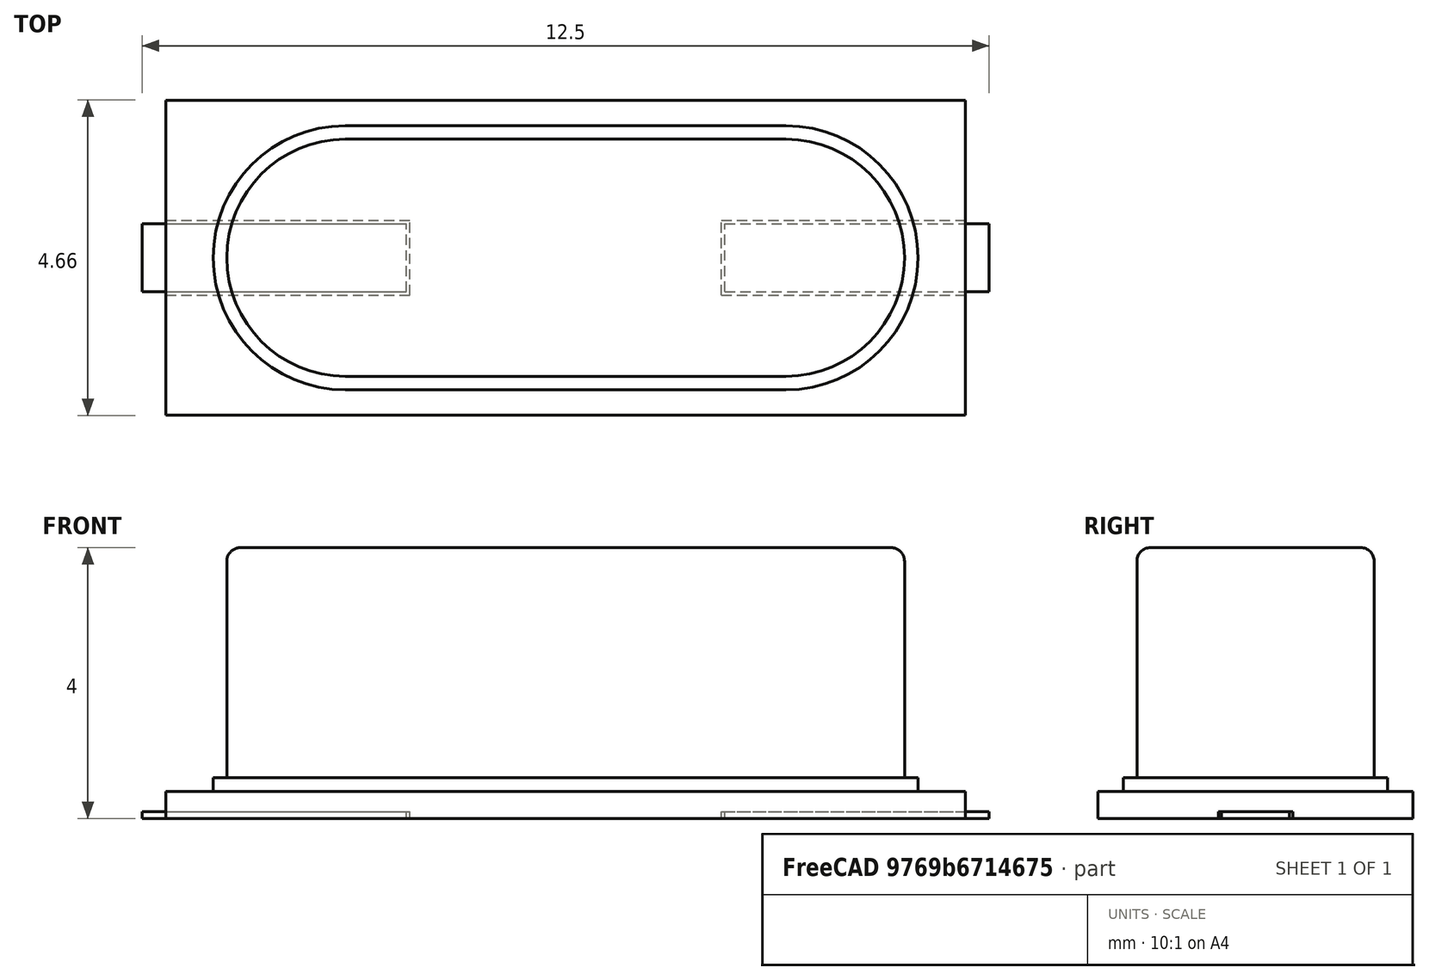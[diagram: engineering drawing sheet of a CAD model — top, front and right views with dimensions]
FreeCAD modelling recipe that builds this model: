
FCSTD DOCUMENT  (FreeCAD 0.18R)
Label: Crystal_SMD_HC49-SD
License: All rights reserved
LicenseURL: http://en.wikipedia.org/wiki/All_rights_reserved
objects: Part::Box×7, Part::Feature×5, Part::Cylinder×4, Part::MultiFuse×2, Part::Cut×2, Part::Fillet×1, App::Part×1, Part::Compound×1
note: 22 computed .brp shape members not serialized (recipe doc carries the construction recipe); baked Part::Feature solids carry a one-line shape summary decoded from their .brp

FEATURE [Part::Box] Box007  label="Pin_R"
  AttacherType = Attacher::AttachEngine3D
  Height = 0.1
  Length = 3.9
  Placement = pos=(2.35,-0.5,0) rot=(0,0,1;0rad)
  Width = 1
FEATURE [Part::Box] Box008  label="Pin_L"
  AttacherType = Attacher::AttachEngine3D
  Height = 0.1
  Length = 3.9
  Placement = pos=(-6.25,-0.5,0) rot=(0,0,1;0rad)
  Width = 1
FEATURE [Part::Box] Box009  label="Cube007"
  AttacherType = Attacher::AttachEngine3D
  Height = 3.4
  Length = 6.5
  Placement = pos=(-3.25,-1.75,0.6) rot=(0,0,1;0rad)
  Width = 3.5
FEATURE [Part::Cylinder] Cylinder004
  Angle = 180
  AttacherType = Attacher::AttachEngine3D
  Height = 3.4
  Placement = pos=(-3.25,0,0.6) rot=(0,0,1;1.5708rad)
  Radius = 1.75
FEATURE [Part::Cylinder] Cylinder005
  Angle = 180
  AttacherType = Attacher::AttachEngine3D
  Height = 3.4
  Placement = pos=(3.25,0,0.6) rot=(0,0,-1;1.5708rad)
  Radius = 1.75
FEATURE [Part::Box] Box010  label="Cube008"
  AttacherType = Attacher::AttachEngine3D
  Height = 0.2
  Length = 6.5
  Placement = pos=(-3.25,-1.95,0.4) rot=(0,0,1;0rad)
  Width = 3.9
FEATURE [Part::Cylinder] Cylinder006
  Angle = 180
  AttacherType = Attacher::AttachEngine3D
  Height = 0.2
  Placement = pos=(-3.25,0,0.4) rot=(0,0,1;1.5708rad)
  Radius = 1.95
FEATURE [Part::Cylinder] Cylinder007
  Angle = 180
  AttacherType = Attacher::AttachEngine3D
  Height = 0.2
  Placement = pos=(3.25,0,0.4) rot=(0,0,-1;1.5708rad)
  Radius = 1.95
FEATURE [Part::MultiFuse] Fusion001
  Shapes = -> [Box009,Cylinder005,Cylinder004,Box010,Cylinder006,Cylinder007]
FEATURE [Part::Fillet] Fillet001  label="Cap"
  Base = -> Fusion001
  Edges = 4 edges r=0.2: [Edge3,Edge8,Edge13,Edge16]
FEATURE [Part::Box] Box011  label="Cube009"
  AttacherType = Attacher::AttachEngine3D
  Height = 0.4
  Length = 11.8
  Placement = pos=(-5.9,-2.325,0) rot=(0,0,1;0rad)
  Width = 4.65
FEATURE [Part::Box] Box012  label="Cube010"
  AttacherType = Attacher::AttachEngine3D
  Height = 0.1
  Length = 4
  Placement = pos=(2.3,-0.55,0) rot=(0,0,1;0rad)
  Width = 1.1
FEATURE [Part::Cut] Cut003
  Base = -> Box011
  Tool = -> Box012
FEATURE [Part::Box] Box013  label="Cube011"
  AttacherType = Attacher::AttachEngine3D
  Height = 0.1
  Length = 4
  Placement = pos=(-6.3,-0.55,0) rot=(0,0,1;0rad)
  Width = 1.1
FEATURE [Part::Cut] Cut002  label="Base"
  Base = -> Cut003
  Tool = -> Box013
FEATURE [App::Part] Part  label="Crystal"
  Group = -> [Box007,Box008,Cylinder005,Fusion001,Box009,Cylinder006,Cylinder007,Box010,Cylinder004,Fillet001,Cut003,Box013,Box012,Box011,Cut002]
  Origin = -> Origin
FEATURE [Part::Feature] Box007_cp  label="Pin_R_cp"
  Placement = pos=(2.35,-0.5,0) rot=(0,0,1;0rad)
  shape: bbox 3.9 x 1 x 0.1 mm, 6 faces (baked)
FEATURE [Part::Feature] Box008_cp  label="Pin_L_cp"
  Placement = pos=(-6.25,-0.5,0) rot=(0,0,1;0rad)
  shape: bbox 3.9 x 1 x 0.1 mm, 6 faces (baked)
FEATURE [Part::Feature] Fillet001_cp  label="Cap_cp"
  shape: bbox 10.4 x 3.9 x 3.6 mm, 22 faces (baked)
FEATURE [Part::Feature] Cut002_cp  label="Base_cp"
  shape: bbox 11.8 x 4.65 x 0.4 mm, 14 faces (baked)
FEATURE [Part::Compound] Crystal_cp
  Links = -> [Box007_cp,Box008_cp,Fillet001_cp,Cut002_cp]
FEATURE [Part::MultiFuse] Crystal_mp_cp  label="Crystal_fd"
  Shapes = -> [Crystal_cp]
FEATURE [Part::Feature] Shape  label="Crystal_SMD_HC49-SD"
  shape: bbox 12.5 x 4.65 x 4 mm, 45 faces (baked)
